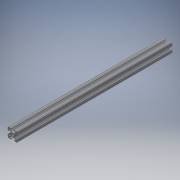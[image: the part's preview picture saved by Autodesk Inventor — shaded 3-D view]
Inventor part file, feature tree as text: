
AUTODESK INVENTOR PART (.ipt)
format: ipt  version: 2018 (Build 220112000, 112)  size: 225,792 bytes
history: native  units: in
note: dims shown in document units (in); Inventor stores cm internally (conversion verified against a paired STEP export)
features: extrude x1, sketch x1
ambient origin geometry x8: Origin, YZ Plane, XZ Plane, XY Plane, X Axis, Y Axis, Z Axis, Center Point
bodies: Solid1 (feature_tree)
feature tree (2):
  extrude  "Extrusion1"  [1 undecoded]
  sketch  "Sketch1"  dims[d0=16.0in d1=0.0in]
note: 1 required parameter value undecoded (feature->parameter linkage not recoverable at this tier; creation-order binding heuristic only, values carry confidence <= 0.55)
